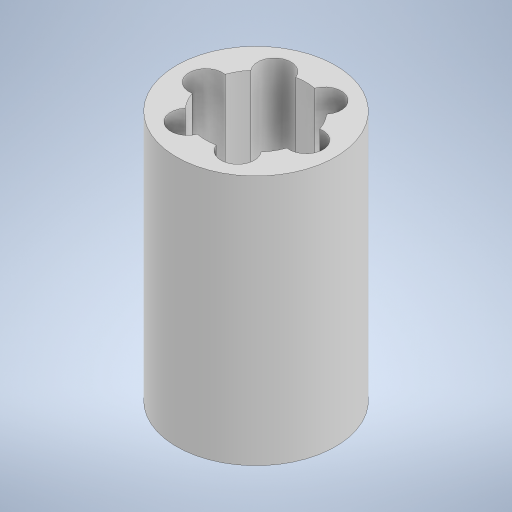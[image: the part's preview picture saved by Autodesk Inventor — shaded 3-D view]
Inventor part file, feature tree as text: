
AUTODESK INVENTOR PART (.ipt)
format: ipt  version: 2023 (Build 270158000, 158)  size: 235,520 bytes
history: native  units: mm
features: extrude x1, sketch x1
ambient origin geometry x8: Origin, YZ Plane, XZ Plane, XY Plane, X Axis, Y Axis, Z Axis, Center Point
bodies: Solid1 (feature_tree)
feature tree (2):
  extrude  "Extrusion1"  Depth=6.0mm
  sketch  "Sketch1"  dims[d0=19.0mm d1=12.0mm d2=4.0mm d3=30.0mm d4=0.0mm d5=60.0mm d7=360.0deg d9=6.0mm d10=5.196152mm d11=3.0mm d12=3.0mm]
